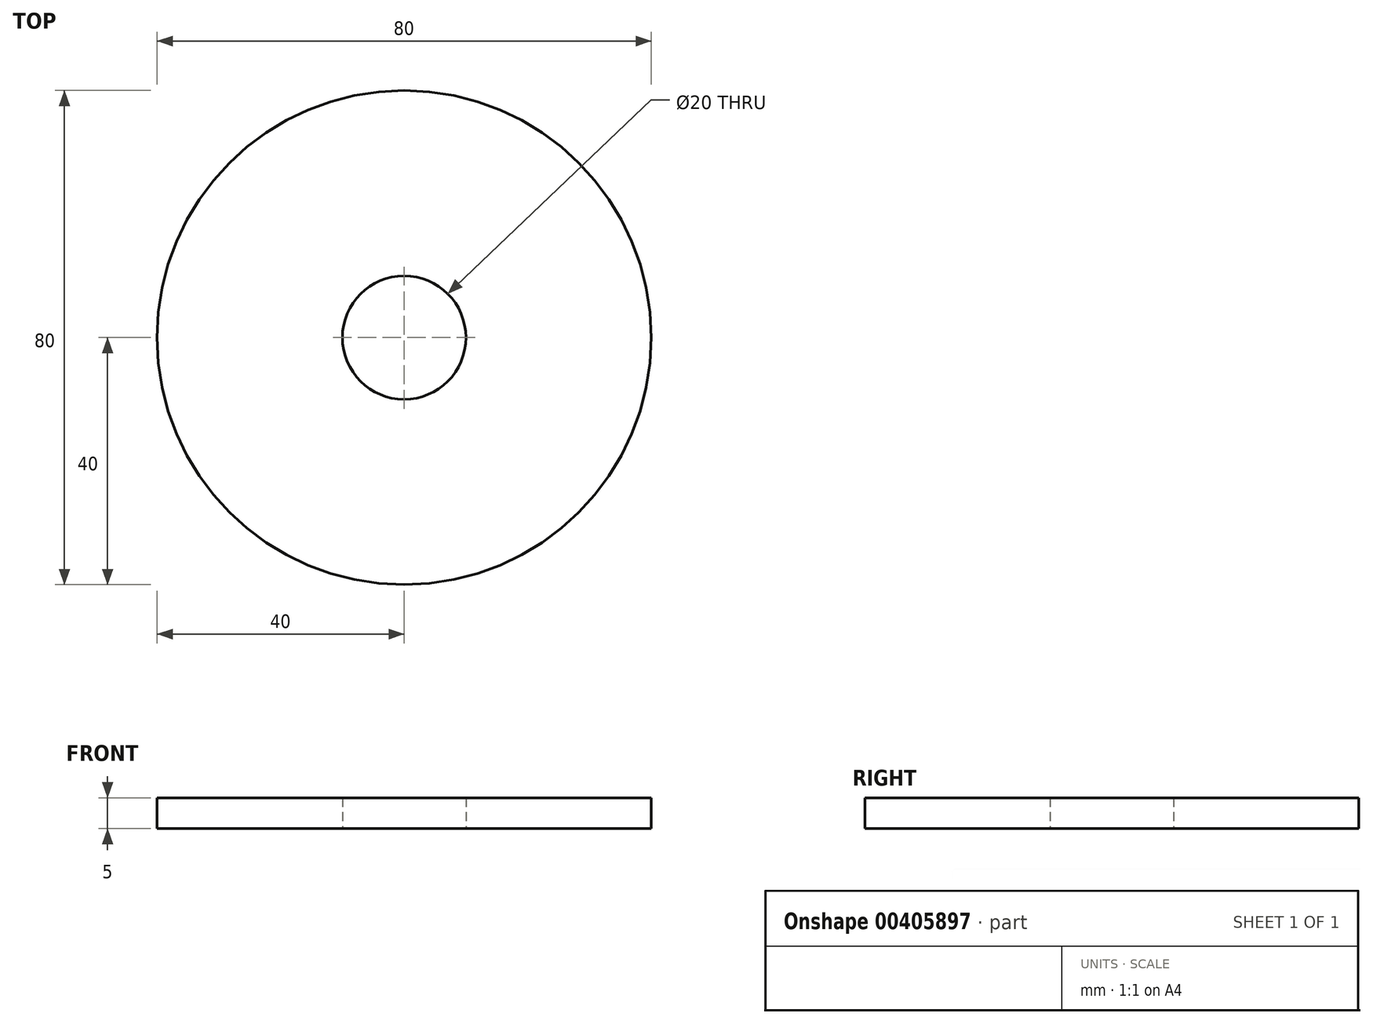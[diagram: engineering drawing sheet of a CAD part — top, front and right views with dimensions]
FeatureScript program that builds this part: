
annotation { "Feature Type Name" : "Feature", "Feature Type Description" : "" }
export const myFeature = defineFeature(function(context is Context, id is Id, definition is map)
    precondition{}
    {
        {
            var Q0;
            Q0=qCreatedBy(makeId("Top.planeOp"),FACE);
            var sketch = newSketch(context, id + "F0", { "sketchPlane" : qUnion([Q0])});
            skCircle(sketch, "E0", {"center": v(0, 0) * mm, "radius": 10 * mm});
            skCircle(sketch, "E1.0", {"center": v(0, 0) * mm, "radius": 40 * mm});
            skSolve(sketch);
        }
        {
            var Q0;
            Q0=makeQuery(id+"F0.imprint","IMPRINT",FACE,{"disambiguationData":[TD([[makeQuery(id+"F0.imprint","IMPRINT",EDGE,{"derivedFrom":sQuery(id+"F0.wireOp",EDGE,"E0")}),-1.0]])]});
            extrude(context, id + "F1", {"entities" : qUnion([Q0]), "depth" : 5 * mm});
        }
    });
